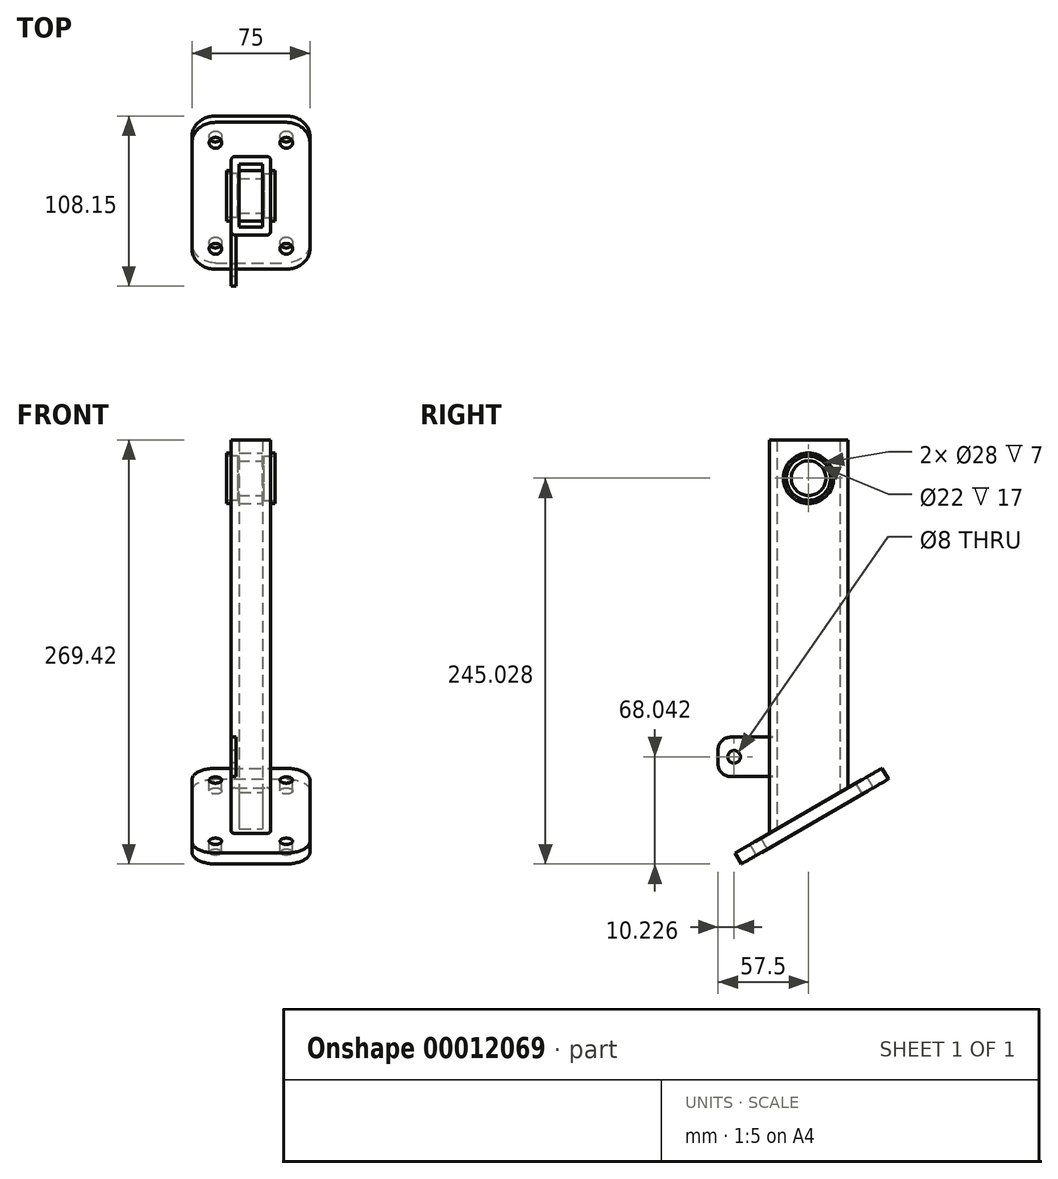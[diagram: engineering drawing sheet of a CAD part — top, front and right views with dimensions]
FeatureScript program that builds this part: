
annotation { "Feature Type Name" : "Feature", "Feature Type Description" : "" }
export const myFeature = defineFeature(function(context is Context, id is Id, definition is map)
    precondition{}
    {
        {
            var Q0;
            Q0=qCreatedBy(makeId("Top.planeOp"),FACE);
            var sketch = newSketch(context, id + "F0", { "sketchPlane" : qUnion([Q0])});
            skLineSegment(sketch, "E0.bottom", {"start": v(22.5, -20) * mm, "end": v(42.5, -20) * mm});
            skLineSegment(sketch, "E0.top", {"start": v(22.5, -70) * mm, "end": v(42.5, -70) * mm});
            skLineSegment(sketch, "E0.left", {"start": v(20, -22.5) * mm, "end": v(20, -67.5) * mm});
            skLineSegment(sketch, "E0.right", {"start": v(45, -22.5) * mm, "end": v(45, -67.5) * mm});
            skPoint(sketch, "E1.visualSharp", {"position": v(20, -20) * mm});
            skArc(sketch, "E1.filletArc", {"start": v(22.5, -20) * mm, "mid": v(20.73, -20.73) * mm, "end": v(20, -22.5) * mm});
            skPoint(sketch, "E2.visualSharp", {"position": v(45, -20) * mm});
            skArc(sketch, "E2.filletArc", {"start": v(45, -22.5) * mm, "mid": v(44.27, -20.73) * mm, "end": v(42.5, -20) * mm});
            skPoint(sketch, "E3.visualSharp", {"position": v(45, -70) * mm});
            skArc(sketch, "E3.filletArc", {"start": v(42.5, -70) * mm, "mid": v(44.27, -69.27) * mm, "end": v(45, -67.5) * mm});
            skPoint(sketch, "E4.visualSharp", {"position": v(20, -70) * mm});
            skArc(sketch, "E4.filletArc", {"start": v(20, -67.5) * mm, "mid": v(20.73, -69.27) * mm, "end": v(22.5, -70) * mm});
            skLineSegment(sketch, "E5.0", {"start": v(40, -25) * mm, "end": v(40, -65) * mm});
            skLineSegment(sketch, "E5.1", {"start": v(25, -25) * mm, "end": v(40, -25) * mm});
            skLineSegment(sketch, "E5.2", {"start": v(25, -25) * mm, "end": v(25, -65) * mm});
            skLineSegment(sketch, "E5.3", {"start": v(25, -65) * mm, "end": v(40, -65) * mm});
            skSolve(sketch);
        }
        {
            var Q0;
            Q0 = qSketchRegion(id + "F0", true);
            extrude(context, id + "F1", {"entities" : qUnion([Q0]), "depth" : 250 * mm});
        }
        {
            var Q0;
            Q0=makeQuery(id+"F1.opExtrude","SWEPT_FACE",FACE,{"disambiguationData":[OSD([sQuery(id+"F0.wireOp",EDGE,"E0.left")])]});
            var sketch = newSketch(context, id + "F2", { "sketchPlane" : qUnion([Q0])});
            skCircle(sketch, "E6", {"center": v(45, 225.6) * mm, "radius": 16 * mm});
            skPoint(sketch, "E6.centerSnap0", {"position": v(45, 250) * mm});
            skLineSegment(sketch, "E7", {"start": v(70.02, 0) * mm, "end": v(7.86, 35.89) * mm});
            skLineSegment(sketch, "E8", {"start": v(7.86, 35.89) * mm, "end": v(7.86, 0) * mm});
            skLineSegment(sketch, "E9", {"start": v(7.86, 0) * mm, "end": v(70.02, 0) * mm});
            skSolve(sketch);
        }
        {
            var Q0;
            Q0 = qSketchRegion(id + "F2", true);
            extrude(context, id + "F3", {"entities" : qUnion([Q0]), "operationType" : NewBodyOperationType.REMOVE, "endBound" : BoundingType.THROUGH_ALL, "oppositeDirection" : true, "depth" : 30 * mm});
        }
        {
            var Q0;
            Q0=makeQuery(id+"F3.boolean.opBoolean","COPY",FACE,{"derivedFrom":makeQuery(id+"F3.opExtrude","SWEPT_FACE",FACE,{"disambiguationData":[OSD([sQuery(id+"F2.wireOp",EDGE,"E7")])]})});
            var sketch = newSketch(context, id + "F4", { "sketchPlane" : qUnion([Q0])});
            skLineSegment(sketch, "E10.1", {"start": v(10, -22.12) * mm, "end": v(55, -22.12) * mm});
            skLineSegment(sketch, "E10.2", {"start": v(70, -7.12) * mm, "end": v(70, 70.62) * mm});
            skLineSegment(sketch, "E10.5", {"start": v(10, 85.62) * mm, "end": v(55, 85.62) * mm});
            skLineSegment(sketch, "E10.7", {"start": v(-5, 70.62) * mm, "end": v(-5, -7.12) * mm});
            skPoint(sketch, "E11.visualSharp", {"position": v(70, 85.62) * mm});
            skArc(sketch, "E11.filletArc", {"start": v(70, 70.62) * mm, "mid": v(65.6, 81.22) * mm, "end": v(55, 85.62) * mm});
            skPoint(sketch, "E12.visualSharp", {"position": v(70, -22.12) * mm});
            skArc(sketch, "E12.filletArc", {"start": v(55, -22.12) * mm, "mid": v(65.6, -17.73) * mm, "end": v(70, -7.12) * mm});
            skPoint(sketch, "E13.visualSharp", {"position": v(-5, -22.12) * mm});
            skArc(sketch, "E13.filletArc", {"start": v(-5, -7.12) * mm, "mid": v(-0.6, -17.73) * mm, "end": v(10, -22.12) * mm});
            skPoint(sketch, "E14.visualSharp", {"position": v(-5, 85.62) * mm});
            skArc(sketch, "E14.filletArc", {"start": v(10, 85.62) * mm, "mid": v(-0.6, 81.22) * mm, "end": v(-5, 70.62) * mm});
            skCircle(sketch, "E15", {"center": v(10, 70.62) * mm, "radius": 4 * mm});
            skCircle(sketch, "E16", {"center": v(10, -7.12) * mm, "radius": 4 * mm});
            skCircle(sketch, "E17", {"center": v(55, -7.12) * mm, "radius": 4 * mm});
            skCircle(sketch, "E18", {"center": v(55, 70.62) * mm, "radius": 4 * mm});
            skSolve(sketch);
        }
        {
            var Q0;
            Q0 = qSketchRegion(id + "F4", true);
            extrude(context, id + "F5", {"entities" : qUnion([Q0]), "operationType" : NewBodyOperationType.ADD, "depth" : 8 * mm});
        }
        {
            var Q0;
            Q0=makeQuery(id+"F1.opExtrude","SWEPT_FACE",FACE,{"disambiguationData":[OSD([sQuery(id+"F0.wireOp",EDGE,"E0.right")])]});
            var sketch = newSketch(context, id + "F6", { "sketchPlane" : qUnion([Q0])});
            skCircle(sketch, "E19", {"center": v(-45, 225.6) * mm, "radius": 16 * mm});
            skCircle(sketch, "E20", {"center": v(-45, 225.6) * mm, "radius": 11 * mm});
            skSolve(sketch);
        }
        {
            var Q0;
            Q0 = qSketchRegion(id + "F6", true);
            extrude(context, id + "F7", {"entities" : qUnion([Q0]), "operationType" : NewBodyOperationType.ADD, "oppositeDirection" : true, "depth" : 28 * mm, "hasSecondDirection" : true, "secondDirectionOppositeDirection" : false, "secondDirectionDepth" : 3 * mm});
        }
        {
            var Q0;
            Q0=makeQuery(id+"F7.opExtrude","CAP_FACE",FACE,{"disambiguationData":[OSD([sQuery(id+"F6.wireOp",EDGE,"E19"),sQuery(id+"F6.wireOp",EDGE,"E20")])],"isStart":true});
            var sketch = newSketch(context, id + "F8", { "sketchPlane" : qUnion([Q0])});
            skCircle(sketch, "E21", {"center": v(-45, 225.6) * mm, "radius": 14 * mm});
            skSolve(sketch);
        }
        {
            var Q0;
            Q0 = qSketchRegion(id + "F8", true);
            extrude(context, id + "F9", {"entities" : qUnion([Q0]), "operationType" : NewBodyOperationType.REMOVE, "oppositeDirection" : true, "depth" : 7 * mm});
        }
        {
            var Q0;
            Q0=makeQuery(id+"F7.opExtrude","CAP_FACE",FACE,{"disambiguationData":[OSD([sQuery(id+"F6.wireOp",EDGE,"E19"),sQuery(id+"F6.wireOp",EDGE,"E20")])],"isStart":false});
            var sketch = newSketch(context, id + "F10", { "sketchPlane" : qUnion([Q0])});
            skCircle(sketch, "E22", {"center": v(45, 225.6) * mm, "radius": 14 * mm});
            skSolve(sketch);
        }
        {
            var Q0;
            Q0 = qSketchRegion(id + "F10", true);
            extrude(context, id + "F11", {"entities" : qUnion([Q0]), "operationType" : NewBodyOperationType.REMOVE, "oppositeDirection" : true, "depth" : 7 * mm});
        }
        {
            var Q0;
            Q0=makeQuery(id+"F1.opExtrude","SWEPT_FACE",FACE,{"disambiguationData":[OSD([sQuery(id+"F0.wireOp",EDGE,"E0.left")])]});
            var sketch = newSketch(context, id + "F12", { "sketchPlane" : qUnion([Q0])});
            skLineSegment(sketch, "E23.bottom", {"start": v(67.5, 61.12) * mm, "end": v(94.5, 61.12) * mm});
            skLineSegment(sketch, "E23.top", {"start": v(67.5, 36.12) * mm, "end": v(94.5, 36.12) * mm});
            skLineSegment(sketch, "E23.left", {"start": v(67.5, 61.12) * mm, "end": v(67.5, 36.12) * mm});
            skLineSegment(sketch, "E23.right", {"start": v(102.5, 53.12) * mm, "end": v(102.5, 44.12) * mm});
            skPoint(sketch, "E24.visualSharp", {"position": v(102.5, 61.12) * mm});
            skArc(sketch, "E24.filletArc", {"start": v(102.5, 53.12) * mm, "mid": v(100.16, 58.78) * mm, "end": v(94.5, 61.12) * mm});
            skPoint(sketch, "E25.visualSharp", {"position": v(102.5, 36.12) * mm});
            skArc(sketch, "E25.filletArc", {"start": v(94.5, 36.12) * mm, "mid": v(100.16, 38.47) * mm, "end": v(102.5, 44.12) * mm});
            skCircle(sketch, "E26", {"center": v(92.27, 48.62) * mm, "radius": 4 * mm});
            skPoint(sketch, "E26.centerSnap0", {"position": v(102.5, 48.62) * mm});
            skSolve(sketch);
        }
        {
            var Q0;
            Q0 = qSketchRegion(id + "F12", true);
            extrude(context, id + "F13", {"entities" : qUnion([Q0]), "operationType" : NewBodyOperationType.ADD, "oppositeDirection" : true, "depth" : 3 * mm});
        }
    });
